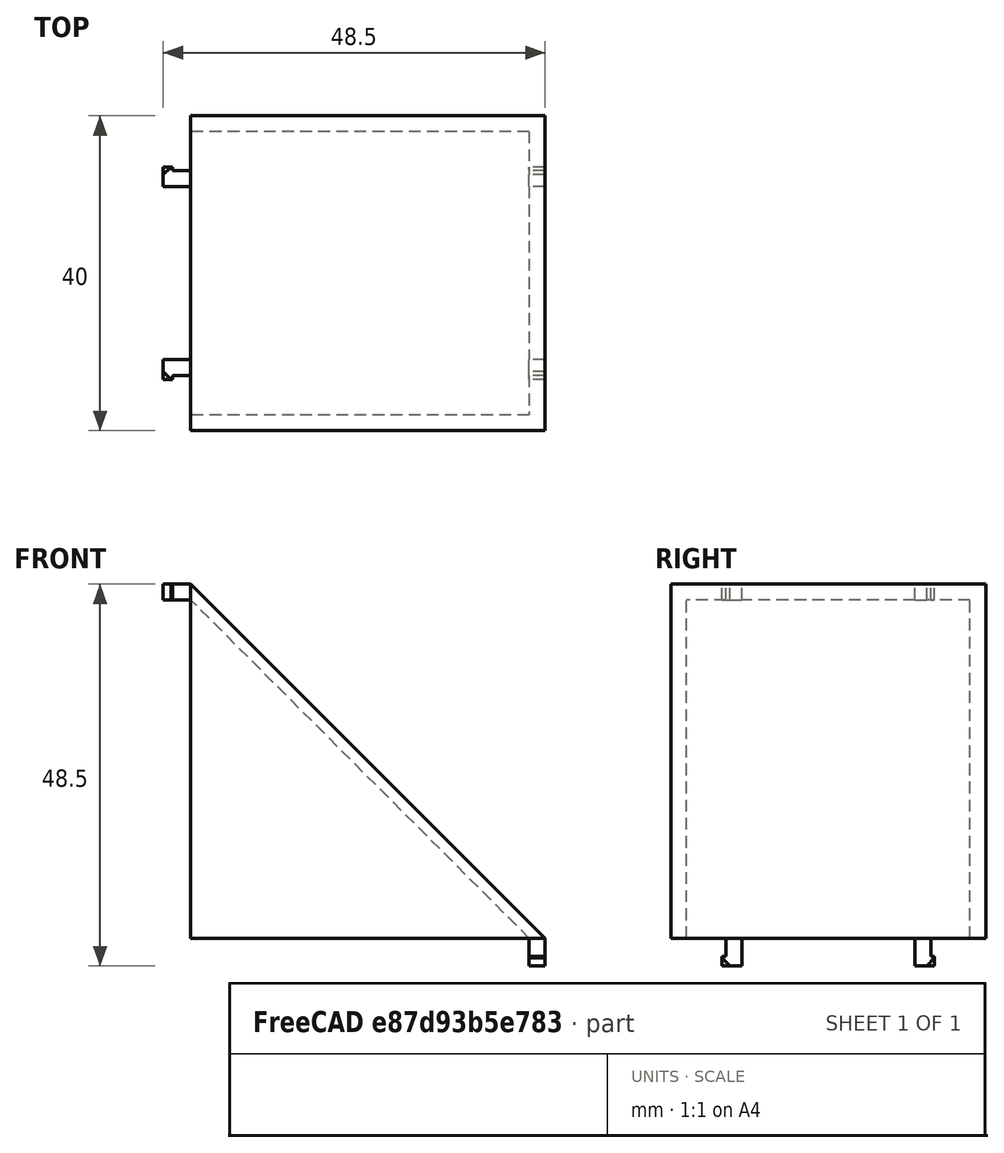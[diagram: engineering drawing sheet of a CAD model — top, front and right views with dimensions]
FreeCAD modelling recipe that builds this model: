
FCSTD DOCUMENT  (FreeCAD 0.18R14555 (Git shallow))
Label: 2040-d-bracket-cover
License: All rights reserved
LicenseURL: http://en.wikipedia.org/wiki/All_rights_reserved
objects: Part::Feature×5, Part::Box×4, Part::MultiFuse×4, Part::Cut×1, Part::Chamfer×1
note: 15 computed .brp shape members not serialized (recipe doc carries the construction recipe); baked Part::Feature solids carry a one-line shape summary decoded from their .brp

FEATURE [Part::Feature] Body001001  label="Body002"
  Placement = pos=(-58,-2,2) rot=(0,0,1;0rad)
  shape: bbox 43 x 36 x 43 mm, 5 faces (baked)
FEATURE [Part::Feature] Body001002  label="Body003"
  Placement = pos=(0,0,5) rot=(0,0,1;0rad)
  shape: bbox 45 x 40 x 45 mm, 5 faces (baked)
FEATURE [Part::Cut] Cut
  Base = -> Body001002
  Tool = -> Body001001
FEATURE [Part::Box] Box  label="Cube"
  AttacherType = Attacher::AttachEngine3D
  Height = 2
  Length = 3.5
  Placement = pos=(-5,0,0) rot=(0,0,1;0rad)
  Width = 2
FEATURE [Part::Box] Box001  label="Cube001"
  AttacherType = Attacher::AttachEngine3D
  Height = 2
  Length = 1.2
  Placement = pos=(-5,0,0) rot=(0,0,1;0rad)
  Width = 2.5
FEATURE [Part::Box] Box002  label="Cube002"
  AttacherType = Attacher::AttachEngine3D
  Height = 2
  Length = 1.2
  Placement = pos=(-5,-6,0) rot=(0,0,1;0rad)
  Width = 2.5
FEATURE [Part::Box] Box003  label="Cube003"
  AttacherType = Attacher::AttachEngine3D
  Height = 2
  Length = 3.5
  Placement = pos=(-5,-5.5,0) rot=(0,0,1;0rad)
  Width = 2
FEATURE [Part::MultiFuse] Fusion
  Placement = pos=(4.5,-27.5,0) rot=(0,0,1;0rad)
  Shapes = -> [Box003,Box002]
FEATURE [Part::MultiFuse] Fusion001
  Placement = pos=(4.5,-9,0) rot=(0,0,1;0rad)
  Shapes = -> [Box001,Box]
FEATURE [Part::MultiFuse] Fusion002
  Placement = pos=(0,0,43) rot=(0,0,1;0rad)
  Shapes = -> [Fusion001,Fusion]
FEATURE [Part::Feature] Fusion002001  label="Fusion003"
  Placement = pos=(48,0,-3) rot=(0,1,0;4.71239rad)
  shape: bbox 2 x 27 x 3.5 mm, 28 faces, 2 solids (baked)
FEATURE [Part::MultiFuse] Fusion002002
  Shapes = -> [Fusion002001,Fusion002,Cut]
FEATURE [Part::Feature] Fusion002002001  label="Fusion002003"
  shape: bbox 48.5 x 40 x 48.5 mm, 40 faces (baked)
FEATURE [Part::Chamfer] Chamfer
  Base = -> Fusion002002001
  Edges = 4 edges r=1: [Edge63,Edge66,Edge75,Edge78]
FEATURE [Part::Feature] Chamfer_solid  label="Chamfer (Solid)"
  shape: bbox 48.5 x 40 x 48.5 mm, 44 faces (baked)
